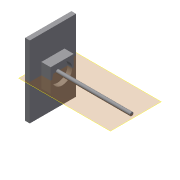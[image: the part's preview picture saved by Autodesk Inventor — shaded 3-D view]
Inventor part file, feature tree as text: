
AUTODESK INVENTOR PART (.ipt)
format: ipt  version: 2019.4 (Build 234330000, 330)  size: 105,984 bytes
history: native  units: mm
features: extrude x4, sketch x4, plane x1, projected_geometry x1
ambient origin geometry x8: Origin, YZ Plane, XZ Plane, XY Plane, X Axis, Y Axis, Z Axis, Center Point
bodies: Solid1 (feature_tree)
feature tree (10):
  extrude  "Extrusion1"  Depth=10.0mm
  extrude  "Extrusion2"  Depth=5.0mm
  extrude  "Extrusion3"  Depth=2.0mm TaperAngle=0.0deg
  extrude  "Extrusion4"  Depth=15.0mm TaperAngle=0.0deg
  plane  "Work Plane1"
  sketch  "Sketch1"  dims[d0=15.5mm d1=10.0mm]
  sketch  "Sketch2"  dims[d2=1.0mm d3=0.0mm d4=5.0mm]
  sketch  "Sketch3"  dims[d5=5.0mm d6=2.0mm d7=0.0mm]
  projected_geometry  "Projected Loop1"
  sketch  "Sketch4"  dims[d8=1.0mm d9=0.0mm d10=15.0mm d11=0.0mm]
